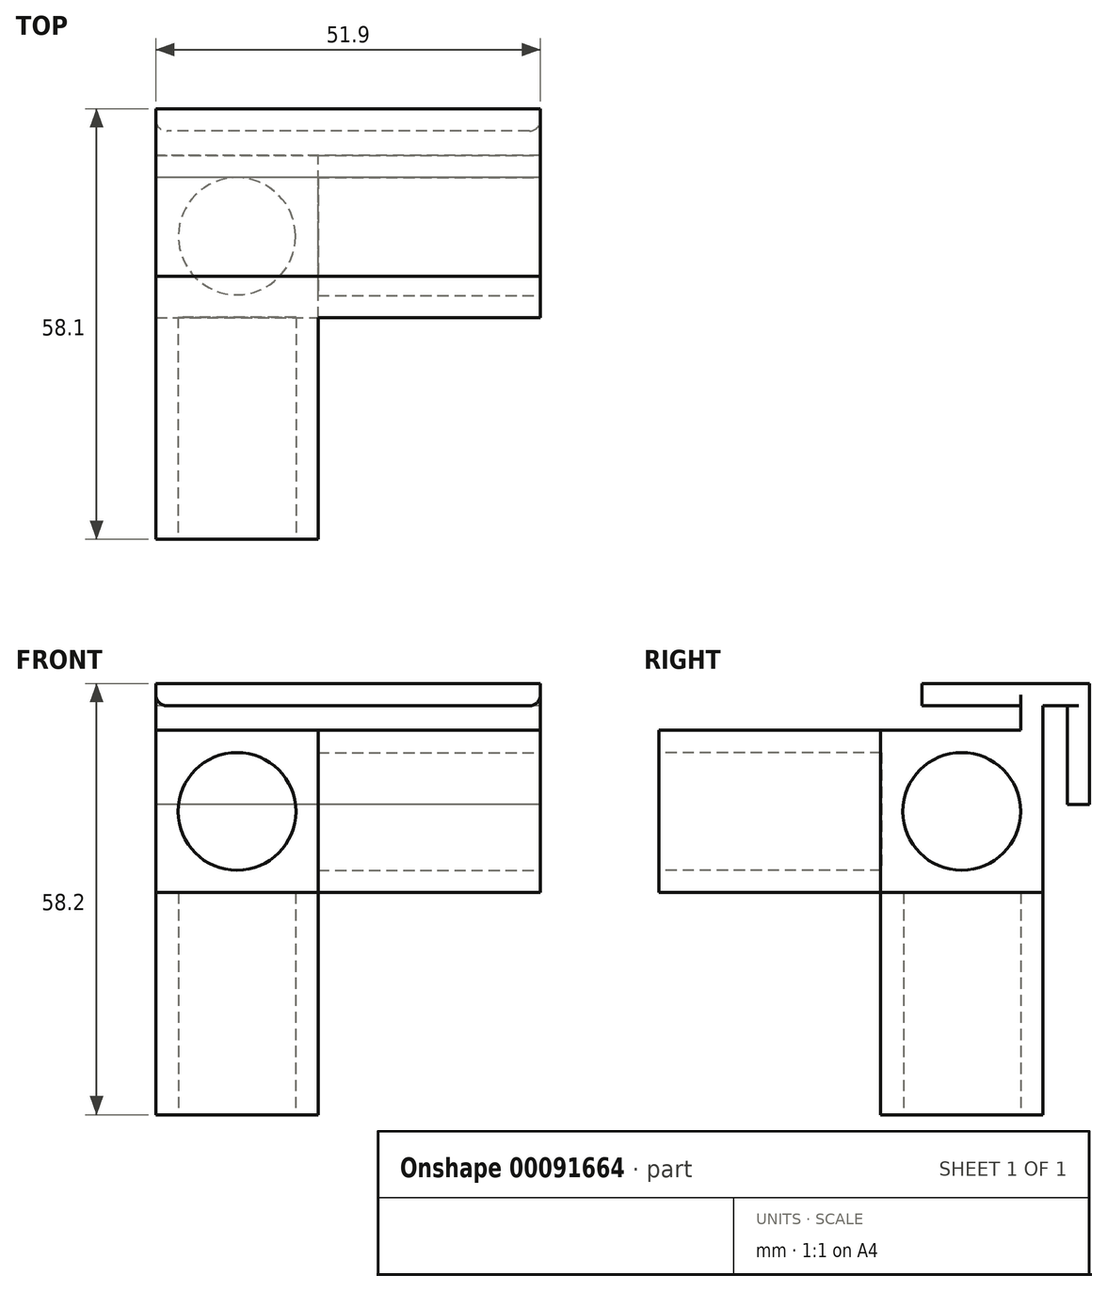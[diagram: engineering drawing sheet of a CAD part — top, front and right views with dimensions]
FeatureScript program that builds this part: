
annotation { "Feature Type Name" : "Feature", "Feature Type Description" : "" }
export const myFeature = defineFeature(function(context is Context, id is Id, definition is map)
    precondition{}
    {
        {
            var Q0;
            Q0=qCreatedBy(makeId("Front.planeOp"),FACE);
            var sketch = newSketch(context, id + "F0", { "sketchPlane" : qUnion([Q0])});
            skLineSegment(sketch, "E0.bottom", {"start": v(-42.3, 45.9) * mm, "end": v(-26.4, 45.9) * mm});
            skLineSegment(sketch, "E0.top", {"start": v(-42.3, 0) * mm, "end": v(-26.4, 0) * mm});
            skLineSegment(sketch, "E0.left", {"start": v(-42.3, 45.9) * mm, "end": v(-42.3, 0) * mm});
            skLineSegment(sketch, "E0.right", {"start": v(-26.4, 45.9) * mm, "end": v(-26.4, 15.9) * mm});
            skLineSegment(sketch, "E1.top", {"start": v(-42.3, 15.9) * mm, "end": v(-26.4, 15.9) * mm});
            skLineSegment(sketch, "E1.left", {"start": v(-42.3, 0) * mm, "end": v(-42.3, 15.9) * mm});
            skLineSegment(sketch, "E1.right", {"start": v(3.6, 0) * mm, "end": v(3.6, 15.9) * mm});
            skLineSegment(sketch, "E2", {"start": v(-26.4, 15.9) * mm, "end": v(-26.4, 0) * mm});
            skLineSegment(sketch, "E3", {"start": v(-26.4, 15.9) * mm, "end": v(3.6, 15.9) * mm});
            skLineSegment(sketch, "E4", {"start": v(-26.4, 0) * mm, "end": v(-26.4, 0) * mm});
            skLineSegment(sketch, "E5", {"start": v(-42.3, 15.9) * mm, "end": v(-42.3, 15.9) * mm});
            skLineSegment(sketch, "E6", {"start": v(-26.4, 0) * mm, "end": v(3.6, 0) * mm});
            skLineSegment(sketch, "E7.0", {"start": v(-45.3, 48.9) * mm, "end": v(-45.3, -3) * mm});
            skLineSegment(sketch, "E7.1", {"start": v(-45.3, -3) * mm, "end": v(-23.4, -3) * mm});
            skLineSegment(sketch, "E7.2", {"start": v(-23.4, 48.9) * mm, "end": v(-23.4, 18.9) * mm});
            skLineSegment(sketch, "E7.3", {"start": v(-23.4, 18.9) * mm, "end": v(6.6, 18.9) * mm});
            skLineSegment(sketch, "E7.4", {"start": v(6.6, -3) * mm, "end": v(6.6, 18.9) * mm});
            skLineSegment(sketch, "E7.5", {"start": v(-45.3, 48.9) * mm, "end": v(-23.4, 48.9) * mm});
            skLineSegment(sketch, "E7.6", {"start": v(-23.4, -3) * mm, "end": v(6.6, -3) * mm});
            skPoint(sketch, "E8", {"position": v(-34.36, 7.95) * mm});
            skPoint(sketch, "E8.positionSnap0", {"position": v(-26.4, 7.95) * mm});
            skPoint(sketch, "E8.positionSnap1", {"position": v(-34.36, 15.9) * mm});
            skCircle(sketch, "E9", {"center": v(-34.36, 7.95) * mm, "radius": 7.95 * mm});
            skLineSegment(sketch, "E10", {"start": v(-23.4, 18.9) * mm, "end": v(-45.3, 18.9) * mm});
            skLineSegment(sketch, "E11", {"start": v(-23.4, 18.9) * mm, "end": v(-23.4, -3) * mm});
            skSolve(sketch);
        }
        {
            var Q0;
            {var subQ1=sQuery(id+"F0.wireOp",EDGE,"E1.top");var subQ3=sQuery(id+"F0.wireOp",EDGE,"E9");var subQ4=makeQuery(id+"F0.imprint","INTERSECT",VERTEX,{"derivedFrom":[subQ1,subQ3]});Q0=makeQuery(id+"F0.imprint","IMPRINT",FACE,{"disambiguationData":[TD([[makeQuery(id+"F0.imprint","IMPRINT",EDGE,{"disambiguationData":[TD([[subQ4,-1.0]])],"derivedFrom":subQ3}),-1.0]])]});}
            var Q1;
            {var subQ0=sQuery(id+"F0.wireOp",EDGE,"E9");var subQ1=makeQuery(id+"F0.imprint","INTERSECT",VERTEX,{"derivedFrom":[sQuery(id+"F0.wireOp",EDGE,"E1.top"),subQ0]});Q1=makeQuery(id+"F0.imprint","IMPRINT",FACE,{"disambiguationData":[TD([[makeQuery(id+"F0.imprint","IMPRINT",EDGE,{"disambiguationData":[TD([[subQ1,1.0]])],"derivedFrom":subQ0}),1.0]])]});}
            var Q2;
            {var subQ5=sQuery(id+"F0.wireOp",EDGE,"E0.bottom");Q2=makeQuery(id+"F0.imprint","IMPRINT",FACE,{"disambiguationData":[TD([[makeQuery(id+"F0.imprint","IMPRINT",EDGE,{"derivedFrom":subQ5}),1.0]])]});}
            var Q3;
            {var subQ0=sQuery(id+"F0.wireOp",EDGE,"E1.right");Q3=makeQuery(id+"F0.imprint","IMPRINT",FACE,{"disambiguationData":[TD([[makeQuery(id+"F0.imprint","IMPRINT",EDGE,{"derivedFrom":subQ0}),1.0]])]});}
            var Q4;
            {var subQ0=sQuery(id+"F0.wireOp",EDGE,"E0.bottom");Q4=makeQuery(id+"F0.imprint","IMPRINT",FACE,{"disambiguationData":[TD([[makeQuery(id+"F0.imprint","IMPRINT",EDGE,{"derivedFrom":subQ0}),-1.0]])]});}
            var Q5;
            {var subQ0=sQuery(id+"F0.wireOp",EDGE,"E1.left");var subQ1=sQuery(id+"F0.wireOp",EDGE,"E0.top");var subQ2=makeQuery(id+"F0.imprint","INTERSECT",VERTEX,{"derivedFrom":[subQ1,subQ0]});Q5=makeQuery(id+"F0.imprint","IMPRINT",FACE,{"disambiguationData":[TD([[makeQuery(id+"F0.imprint","IMPRINT",EDGE,{"disambiguationData":[TD([[subQ2,-1.0]])],"derivedFrom":subQ1}),1.0]])]});}
            var Q6;
            {var subQ1=sQuery(id+"F0.wireOp",EDGE,"E0.top");var subQ3=sQuery(id+"F0.wireOp",EDGE,"E9");var subQ4=makeQuery(id+"F0.imprint","INTERSECT",VERTEX,{"derivedFrom":[subQ1,subQ3]});Q6=makeQuery(id+"F0.imprint","IMPRINT",FACE,{"disambiguationData":[TD([[makeQuery(id+"F0.imprint","IMPRINT",EDGE,{"disambiguationData":[TD([[subQ4,-1.0]])],"derivedFrom":subQ3}),-1.0]])]});}
            var Q7;
            {var subQ1=sQuery(id+"F0.wireOp",EDGE,"E1.top");var subQ3=sQuery(id+"F0.wireOp",EDGE,"E9");var subQ4=makeQuery(id+"F0.imprint","INTERSECT",VERTEX,{"derivedFrom":[subQ1,subQ3]});Q7=makeQuery(id+"F0.imprint","IMPRINT",FACE,{"disambiguationData":[TD([[makeQuery(id+"F0.imprint","IMPRINT",EDGE,{"disambiguationData":[TD([[subQ4,1.0]])],"derivedFrom":subQ3}),-1.0]])]});}
            var Q8;
            {var subQ5=sQuery(id+"F0.wireOp",EDGE,"E1.right");Q8=makeQuery(id+"F0.imprint","IMPRINT",FACE,{"disambiguationData":[TD([[makeQuery(id+"F0.imprint","IMPRINT",EDGE,{"derivedFrom":subQ5}),-1.0]])]});}
            var Q9;
            {var subQ4=sQuery(id+"F0.wireOp",EDGE,"E0.left");var subQ6=sQuery(id+"F0.wireOp",EDGE,"E10");var subQ8=makeQuery(id+"F0.imprint","INTERSECT",VERTEX,{"derivedFrom":[subQ4,subQ6]});Q9=makeQuery(id+"F0.imprint","IMPRINT",FACE,{"disambiguationData":[TD([[makeQuery(id+"F0.imprint","IMPRINT",EDGE,{"disambiguationData":[TD([[subQ8,1.0]])],"derivedFrom":subQ6}),1.0]])]});}
            var Q10;
            {var subQ3=sQuery(id+"F0.wireOp",EDGE,"E11");var subQ5=sQuery(id+"F0.wireOp",EDGE,"E3");var subQ8=makeQuery(id+"F0.imprint","INTERSECT",VERTEX,{"derivedFrom":[subQ5,subQ3]});Q10=makeQuery(id+"F0.imprint","IMPRINT",FACE,{"disambiguationData":[TD([[makeQuery(id+"F0.imprint","IMPRINT",EDGE,{"disambiguationData":[TD([[subQ8,-1.0]])],"derivedFrom":subQ3}),-1.0]])]});}
            var Q11;
            {var subQ14=sQuery(id+"F0.wireOp",EDGE,"E7.1");Q11=makeQuery(id+"F0.imprint","IMPRINT",FACE,{"disambiguationData":[TD([[makeQuery(id+"F0.imprint","IMPRINT",EDGE,{"derivedFrom":subQ14}),1.0]])]});}
            var Q12;
            {var subQ1=sQuery(id+"F0.wireOp",EDGE,"E0.right");var subQ3=sQuery(id+"F0.wireOp",EDGE,"E10");var subQ4=makeQuery(id+"F0.imprint","INTERSECT",VERTEX,{"derivedFrom":[subQ1,subQ3]});Q12=makeQuery(id+"F0.imprint","IMPRINT",FACE,{"disambiguationData":[TD([[makeQuery(id+"F0.imprint","IMPRINT",EDGE,{"disambiguationData":[TD([[subQ4,-1.0]])],"derivedFrom":subQ1}),1.0]])]});}
            extrude(context, id + "F1", {"entities" : qUnion([Q0, Q1, Q2, Q3, Q4, Q5, Q6, Q7, Q8, Q9, Q10, Q11, Q12]), "depth" : (15.9 + 6) * mm});
        }
        {
            var Q0;
            {var subQ14=sQuery(id+"F0.wireOp",EDGE,"E7.1");Q0=makeQuery(id+"F0.imprint","IMPRINT",FACE,{"disambiguationData":[TD([[makeQuery(id+"F0.imprint","IMPRINT",EDGE,{"derivedFrom":subQ14}),1.0]])]});}
            var Q1;
            {var subQ0=sQuery(id+"F0.wireOp",EDGE,"E9");var subQ1=makeQuery(id+"F0.imprint","INTERSECT",VERTEX,{"derivedFrom":[sQuery(id+"F0.wireOp",EDGE,"E1.top"),subQ0]});Q1=makeQuery(id+"F0.imprint","IMPRINT",FACE,{"disambiguationData":[TD([[makeQuery(id+"F0.imprint","IMPRINT",EDGE,{"disambiguationData":[TD([[subQ1,1.0]])],"derivedFrom":subQ0}),1.0]])]});}
            var Q2;
            {var subQ4=sQuery(id+"F0.wireOp",EDGE,"E0.left");var subQ6=sQuery(id+"F0.wireOp",EDGE,"E10");var subQ8=makeQuery(id+"F0.imprint","INTERSECT",VERTEX,{"derivedFrom":[subQ4,subQ6]});Q2=makeQuery(id+"F0.imprint","IMPRINT",FACE,{"disambiguationData":[TD([[makeQuery(id+"F0.imprint","IMPRINT",EDGE,{"disambiguationData":[TD([[subQ8,1.0]])],"derivedFrom":subQ6}),1.0]])]});}
            var Q3;
            {var subQ3=sQuery(id+"F0.wireOp",EDGE,"E11");var subQ5=sQuery(id+"F0.wireOp",EDGE,"E3");var subQ8=makeQuery(id+"F0.imprint","INTERSECT",VERTEX,{"derivedFrom":[subQ5,subQ3]});Q3=makeQuery(id+"F0.imprint","IMPRINT",FACE,{"disambiguationData":[TD([[makeQuery(id+"F0.imprint","IMPRINT",EDGE,{"disambiguationData":[TD([[subQ8,-1.0]])],"derivedFrom":subQ3}),-1.0]])]});}
            var Q4;
            {var subQ1=sQuery(id+"F0.wireOp",EDGE,"E0.right");var subQ3=sQuery(id+"F0.wireOp",EDGE,"E10");var subQ4=makeQuery(id+"F0.imprint","INTERSECT",VERTEX,{"derivedFrom":[subQ1,subQ3]});Q4=makeQuery(id+"F0.imprint","IMPRINT",FACE,{"disambiguationData":[TD([[makeQuery(id+"F0.imprint","IMPRINT",EDGE,{"disambiguationData":[TD([[subQ4,-1.0]])],"derivedFrom":subQ1}),1.0]])]});}
            var Q5;
            {var subQ1=sQuery(id+"F0.wireOp",EDGE,"E1.top");var subQ3=sQuery(id+"F0.wireOp",EDGE,"E9");var subQ4=makeQuery(id+"F0.imprint","INTERSECT",VERTEX,{"derivedFrom":[subQ1,subQ3]});Q5=makeQuery(id+"F0.imprint","IMPRINT",FACE,{"disambiguationData":[TD([[makeQuery(id+"F0.imprint","IMPRINT",EDGE,{"disambiguationData":[TD([[subQ4,1.0]])],"derivedFrom":subQ3}),-1.0]])]});}
            var Q6;
            {var subQ1=sQuery(id+"F0.wireOp",EDGE,"E1.top");var subQ3=sQuery(id+"F0.wireOp",EDGE,"E9");var subQ4=makeQuery(id+"F0.imprint","INTERSECT",VERTEX,{"derivedFrom":[subQ1,subQ3]});Q6=makeQuery(id+"F0.imprint","IMPRINT",FACE,{"disambiguationData":[TD([[makeQuery(id+"F0.imprint","IMPRINT",EDGE,{"disambiguationData":[TD([[subQ4,-1.0]])],"derivedFrom":subQ3}),-1.0]])]});}
            var Q7;
            {var subQ0=sQuery(id+"F0.wireOp",EDGE,"E1.left");var subQ1=sQuery(id+"F0.wireOp",EDGE,"E0.top");var subQ2=makeQuery(id+"F0.imprint","INTERSECT",VERTEX,{"derivedFrom":[subQ1,subQ0]});Q7=makeQuery(id+"F0.imprint","IMPRINT",FACE,{"disambiguationData":[TD([[makeQuery(id+"F0.imprint","IMPRINT",EDGE,{"disambiguationData":[TD([[subQ2,-1.0]])],"derivedFrom":subQ1}),1.0]])]});}
            var Q8;
            {var subQ1=sQuery(id+"F0.wireOp",EDGE,"E0.top");var subQ3=sQuery(id+"F0.wireOp",EDGE,"E9");var subQ4=makeQuery(id+"F0.imprint","INTERSECT",VERTEX,{"derivedFrom":[subQ1,subQ3]});Q8=makeQuery(id+"F0.imprint","IMPRINT",FACE,{"disambiguationData":[TD([[makeQuery(id+"F0.imprint","IMPRINT",EDGE,{"disambiguationData":[TD([[subQ4,-1.0]])],"derivedFrom":subQ3}),-1.0]])]});}
            extrude(context, id + "F2", {"entities" : qUnion([Q0, Q1, Q2, Q3, Q4, Q5, Q6, Q7, Q8]), "operationType" : NewBodyOperationType.ADD, "depth" : (15.8 + 6 + 30) * mm});
        }
        {
            var Q0;
            Q0=makeQuery(id+"F2.opExtrude","CAP_FACE",FACE,{"disambiguationData":[OSD([sQuery(id+"F0.wireOp",EDGE,"E7.0"),sQuery(id+"F0.wireOp",EDGE,"E7.1"),sQuery(id+"F0.wireOp",EDGE,"E10"),sQuery(id+"F0.wireOp",EDGE,"E11")])],"isStart":false});
            var sketch = newSketch(context, id + "F3", { "sketchPlane" : qUnion([Q0])});
            skCircle(sketch, "E12.0", {"center": v(-34.36, 7.95) * mm, "radius": 7.95 * mm});
            skSolve(sketch);
        }
        {
            var Q0;
            Q0=makeQuery(id+"F1.opExtrude","SWEPT_FACE",FACE,{"disambiguationData":[OSD([sQuery(id+"F0.wireOp",EDGE,"E7.5")])]});
            var sketch = newSketch(context, id + "F4", { "sketchPlane" : qUnion([Q0])});
            skPoint(sketch, "E13", {"position": v(-34.36, -3) * mm});
            skPoint(sketch, "E14", {"position": v(-26.4, -10.9) * mm});
            skPoint(sketch, "E15", {"position": v(-34.36, -10.9) * mm});
            skPoint(sketch, "E16", {"position": v(-62.98, 75) * mm});
            skPoint(sketch, "E17.orphan", {"position": v(-42.3, -3) * mm});
            skPoint(sketch, "E18.orphan", {"position": v(-26.4, -3) * mm});
            skPoint(sketch, "E19.orphan", {"position": v(-26.4, -18.8) * mm});
            skCircle(sketch, "E20", {"center": v(-34.36, -10.9) * mm, "radius": 7.9 * mm});
            skSolve(sketch);
        }
        {
            var Q0;
            Q0=makeQuery(id+"F1.opExtrude","SWEPT_FACE",FACE,{"disambiguationData":[OSD([sQuery(id+"F0.wireOp",EDGE,"E7.4")])]});
            var sketch = newSketch(context, id + "F5", { "sketchPlane" : qUnion([Q0])});
            skLineSegment(sketch, "E21.0", {"start": v(-18.9, 15.9) * mm, "end": v(-3, 15.9) * mm});
            skLineSegment(sketch, "E21.1", {"start": v(-18.9, 0) * mm, "end": v(-18.9, 15.9) * mm});
            skLineSegment(sketch, "E21.2", {"start": v(-18.9, 0) * mm, "end": v(-3, 0) * mm});
            skLineSegment(sketch, "E21.3", {"start": v(-3, 0) * mm, "end": v(-3, 15.9) * mm});
            skCircle(sketch, "E22", {"center": v(-10.95, 7.95) * mm, "radius": 7.95 * mm});
            skPoint(sketch, "E22.centerSnap0", {"position": v(-10.95, 0) * mm});
            skPoint(sketch, "E22.centerSnap1", {"position": v(-3, 7.95) * mm});
            skSolve(sketch);
        }
        {
            var Q0;
            Q0=makeQuery(id+"F3.imprint","IMPRINT",FACE,{"disambiguationData":[TD([[makeQuery(id+"F3.imprint","IMPRINT",EDGE,{"derivedFrom":sQuery(id+"F3.wireOp",EDGE,"E12.0")}),1.0]])]});
            extrude(context, id + "F6", {"entities" : qUnion([Q0]), "operationType" : NewBodyOperationType.REMOVE, "oppositeDirection" : true, "depth" : 30 * mm});
        }
        {
            var Q0;
            {var subQ0=sQuery(id+"F5.wireOp",EDGE,"E22");var subQ1=makeQuery(id+"F5.imprint","INTERSECT",VERTEX,{"derivedFrom":[sQuery(id+"F5.wireOp",EDGE,"E21.1"),subQ0]});Q0=makeQuery(id+"F5.imprint","IMPRINT",FACE,{"disambiguationData":[TD([[makeQuery(id+"F5.imprint","IMPRINT",EDGE,{"disambiguationData":[TD([[subQ1,1.0]])],"derivedFrom":subQ0}),1.0]])]});}
            extrude(context, id + "F7", {"entities" : qUnion([Q0]), "operationType" : NewBodyOperationType.REMOVE, "oppositeDirection" : true, "depth" : 30 * mm});
        }
        {
            var Q0;
            Q0=makeQuery(id+"F4.imprint","IMPRINT",FACE,{"disambiguationData":[TD([[makeQuery(id+"F4.imprint","IMPRINT",EDGE,{"derivedFrom":sQuery(id+"F4.wireOp",EDGE,"E20")}),1.0]])]});
            var Q1;
            Q1=sQuery(id+"F4.wireOp",EDGE,"E20");
            extrude(context, id + "F8", {"entities" : qUnion([Q0]), "operationType" : NewBodyOperationType.REMOVE, "surfaceEntities" : qUnion([Q1]), "oppositeDirection" : true, "depth" : 30 * mm});
        }
        {
            var Q0;
            {var subQ0=sQuery(id+"F0.wireOp",EDGE,"E7.0");Q0=makeQuery(id+"F2.boolean.opBoolean","MERGE",FACE,{"derivedFrom":[makeQuery(id+"F1.opExtrude","SWEPT_FACE",FACE,{"disambiguationData":[OSD([subQ0])]}),makeQuery(id+"F2.opExtrude","SWEPT_FACE",FACE,{"disambiguationData":[OSD([subQ0])]})]});}
            var sketch = newSketch(context, id + "F9", { "sketchPlane" : qUnion([Q0])});
            skLineSegment(sketch, "E23.0.0", {"start": v(0, -3) * mm, "end": v(51.8, -3) * mm});
            skLineSegment(sketch, "E23.0.2", {"start": v(51.8, 18.9) * mm, "end": v(21.9, 18.9) * mm});
            skLineSegment(sketch, "E23.0.4", {"start": v(21.9, 48.9) * mm, "end": v(0, 48.9) * mm});
            skLineSegment(sketch, "E24", {"start": v(0, -3) * mm, "end": v(0, -9.3) * mm});
            skLineSegment(sketch, "E25", {"start": v(0, -9.3) * mm, "end": v(16.3, -9.3) * mm});
            skLineSegment(sketch, "E26", {"start": v(16.3, -9.3) * mm, "end": v(16.3, -6.3) * mm});
            skLineSegment(sketch, "E27", {"start": v(16.3, -6.3) * mm, "end": v(3, -6.3) * mm});
            skLineSegment(sketch, "E28", {"start": v(3, -6.3) * mm, "end": v(3, -3) * mm});
            skLineSegment(sketch, "E29", {"start": v(0, -9.3) * mm, "end": v(-3.3, -9.3) * mm});
            skLineSegment(sketch, "E30", {"start": v(-3.3, -9.3) * mm, "end": v(-3.3, -6.3) * mm});
            skLineSegment(sketch, "E31", {"start": v(-3.3, -6.3) * mm, "end": v(0, -6.3) * mm});
            skLineSegment(sketch, "E32", {"start": v(-3.3, -9.3) * mm, "end": v(-6.3, -9.3) * mm});
            skLineSegment(sketch, "E33", {"start": v(-6.3, -9.3) * mm, "end": v(-6.3, 7) * mm});
            skLineSegment(sketch, "E34", {"start": v(-6.3, 7) * mm, "end": v(-3.3, 7) * mm});
            skLineSegment(sketch, "E35", {"start": v(-3.3, 7) * mm, "end": v(-3.3, -6.3) * mm});
            skSolve(sketch);
        }
        {
            var Q0;
            {var subQ0=sQuery(id+"F9.wireOp",EDGE,"E25");Q0=makeQuery(id+"F9.imprint","IMPRINT",FACE,{"disambiguationData":[TD([[makeQuery(id+"F9.imprint","IMPRINT",EDGE,{"derivedFrom":subQ0}),1.0]])]});}
            var Q1;
            {var subQ0=sQuery(id+"F9.wireOp",EDGE,"E29");Q1=makeQuery(id+"F9.imprint","IMPRINT",FACE,{"disambiguationData":[TD([[makeQuery(id+"F9.imprint","IMPRINT",EDGE,{"derivedFrom":subQ0}),-1.0]])]});}
            var Q2;
            Q2=makeQuery(id+"F9.imprint","IMPRINT",FACE,{"disambiguationData":[TD([[makeQuery(id+"F9.imprint","IMPRINT",EDGE,{"derivedFrom":sQuery(id+"F9.wireOp",EDGE,"E30")}),1.0]])]});
            extrude(context, id + "F10", {"entities" : qUnion([Q0, Q1, Q2]), "operationType" : NewBodyOperationType.ADD, "oppositeDirection" : true, "depth" : (6 + 15.9 + 30) * mm});
        }
        {
            var Q0;
            Q0=makeQuery(id+"F10.opExtrude","CAP_EDGE",EDGE,{"disambiguationData":[OSD([sQuery(id+"F9.wireOp",EDGE,"E27")])],"isStart":true});
            var Q1;
            Q1=makeQuery(id+"F10.opExtrude","CAP_EDGE",EDGE,{"disambiguationData":[OSD([sQuery(id+"F9.wireOp",EDGE,"E27")])],"isStart":false});
            var Q2;
            Q2=makeQuery(id+"F10.opExtrude","CAP_EDGE",EDGE,{"disambiguationData":[OSD([sQuery(id+"F9.wireOp",EDGE,"E35")])],"isStart":true});
            var Q3;
            Q3=makeQuery(id+"F10.opExtrude","CAP_EDGE",EDGE,{"disambiguationData":[OSD([sQuery(id+"F9.wireOp",EDGE,"E35")])],"isStart":false});
            fillet(context, id + "F11", {"entities" : qUnion([Q0, Q1, Q2, Q3]), "radius" : 1.5 * mm, "tangentPropagation" : true, "allowEdgeOverflow" : false});
        }
        {
            var Q0;
            Q0=makeQuery(id+"F1.opExtrude","SWEPT_BODY",BODY,{"disambiguationData":[OSD([sQuery(id+"F0.wireOp",EDGE,"E7.0"),sQuery(id+"F0.wireOp",EDGE,"E7.1"),sQuery(id+"F0.wireOp",EDGE,"E7.2"),sQuery(id+"F0.wireOp",EDGE,"E7.3"),sQuery(id+"F0.wireOp",EDGE,"E7.4"),sQuery(id+"F0.wireOp",EDGE,"E7.5"),sQuery(id+"F0.wireOp",EDGE,"E7.6")])]});
            var Q1;
            Q1=makeQuery(id+"F10.opExtrude","SWEPT_FACE",FACE,{"disambiguationData":[OSD([sQuery(id+"F9.wireOp",EDGE,"E25"),sQuery(id+"F9.wireOp",EDGE,"E29"),sQuery(id+"F9.wireOp",EDGE,"E32")])]});
            mirror(context, id + "F12", {"entities" : qUnion([Q0]), "mirrorPlane" : qUnion([Q1])});
        }
        {
            var Q0;
            Q0=makeQuery(id+"F1.opExtrude","SWEPT_BODY",BODY,{"disambiguationData":[OSD([sQuery(id+"F0.wireOp",EDGE,"E7.0"),sQuery(id+"F0.wireOp",EDGE,"E7.1"),sQuery(id+"F0.wireOp",EDGE,"E7.2"),sQuery(id+"F0.wireOp",EDGE,"E7.3"),sQuery(id+"F0.wireOp",EDGE,"E7.4"),sQuery(id+"F0.wireOp",EDGE,"E7.5"),sQuery(id+"F0.wireOp",EDGE,"E7.6")])]});
            deleteBodies(context, id + "F13", {"entities" : qUnion([Q0])});
        }
    });
